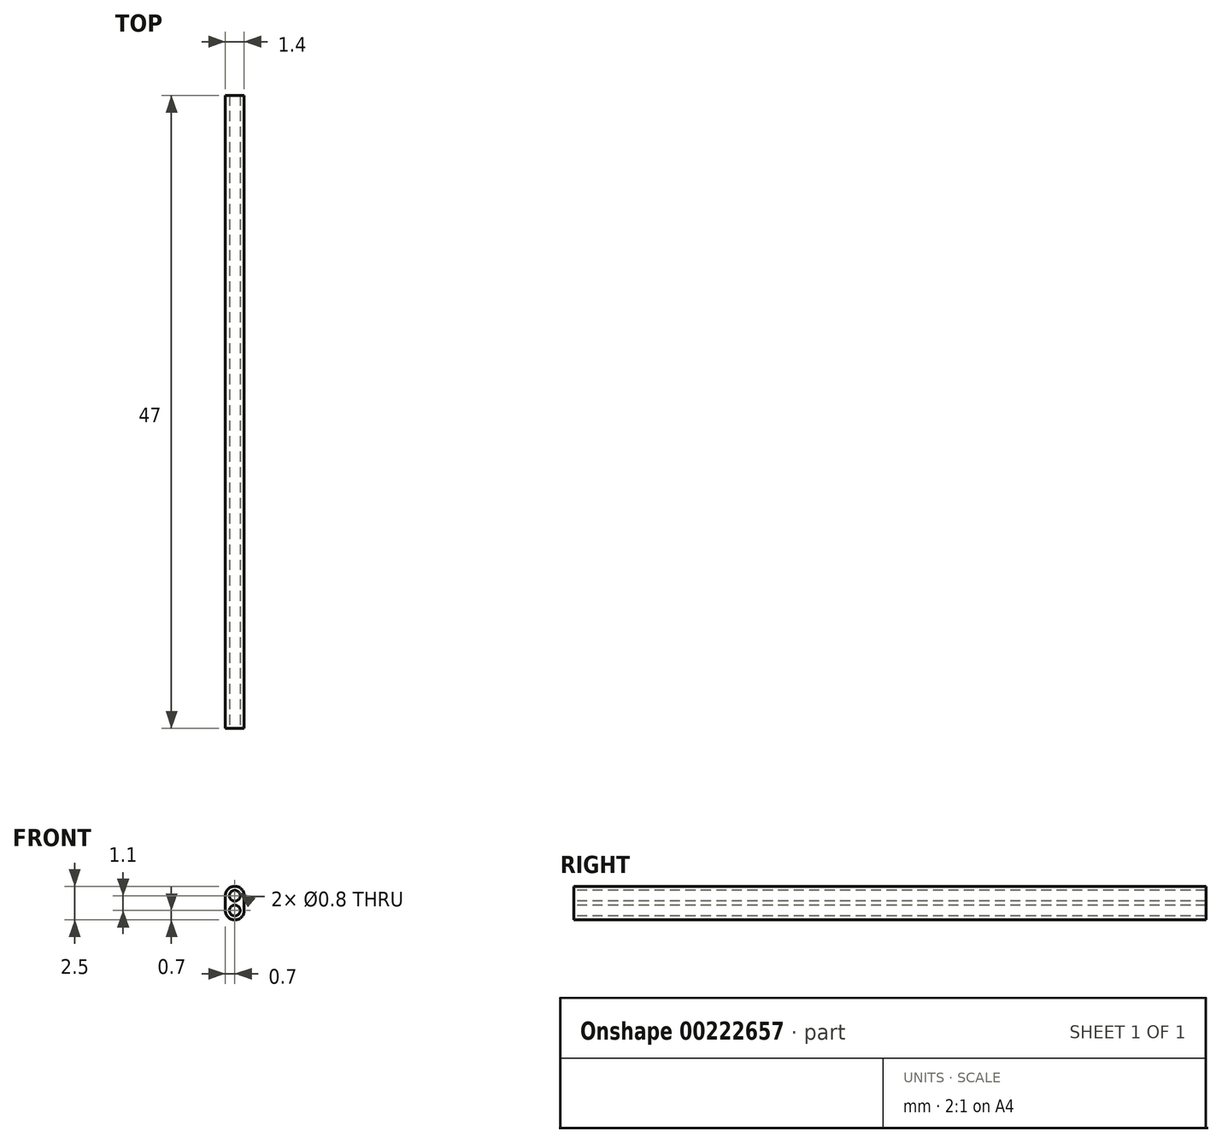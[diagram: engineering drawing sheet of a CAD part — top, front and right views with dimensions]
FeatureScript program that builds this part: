
annotation { "Feature Type Name" : "Feature", "Feature Type Description" : "" }
export const myFeature = defineFeature(function(context is Context, id is Id, definition is map)
    precondition{}
    {
        {
            var Q0;
            Q0=qCreatedBy(makeId("Front.planeOp"),FACE);
            var sketch = newSketch(context, id + "F0", { "sketchPlane" : qUnion([Q0])});
            skLineSegment(sketch, "E0.left", {"start": v(-0.7, -0.55) * mm, "end": v(-0.7, 0.55) * mm});
            skLineSegment(sketch, "E0.right", {"start": v(0.7, -0.55) * mm, "end": v(0.7, 0.55) * mm});
            skPoint(sketch, "E0.middle", {"position": v(0, 0) * mm});
            skCircle(sketch, "E1", {"center": v(0, 0.55) * mm, "radius": 0.4 * mm});
            skCircle(sketch, "E2", {"center": v(0, -0.55) * mm, "radius": 0.4 * mm});
            skArc(sketch, "E3", {"start": v(-0.7, 0.55) * mm, "mid": v(0, 1.25) * mm, "end": v(0.7, 0.55) * mm});
            skArc(sketch, "E4", {"start": v(-0.7, -0.55) * mm, "mid": v(0, -1.25) * mm, "end": v(0.7, -0.55) * mm});
            skSolve(sketch);
        }
        {
            var Q0;
            Q0 = qSketchRegion(id + "F0", true);
            extrude(context, id + "F1", {"entities" : qUnion([Q0]), "oppositeDirection" : true, "depth" : 47 * mm});
        }
    });
